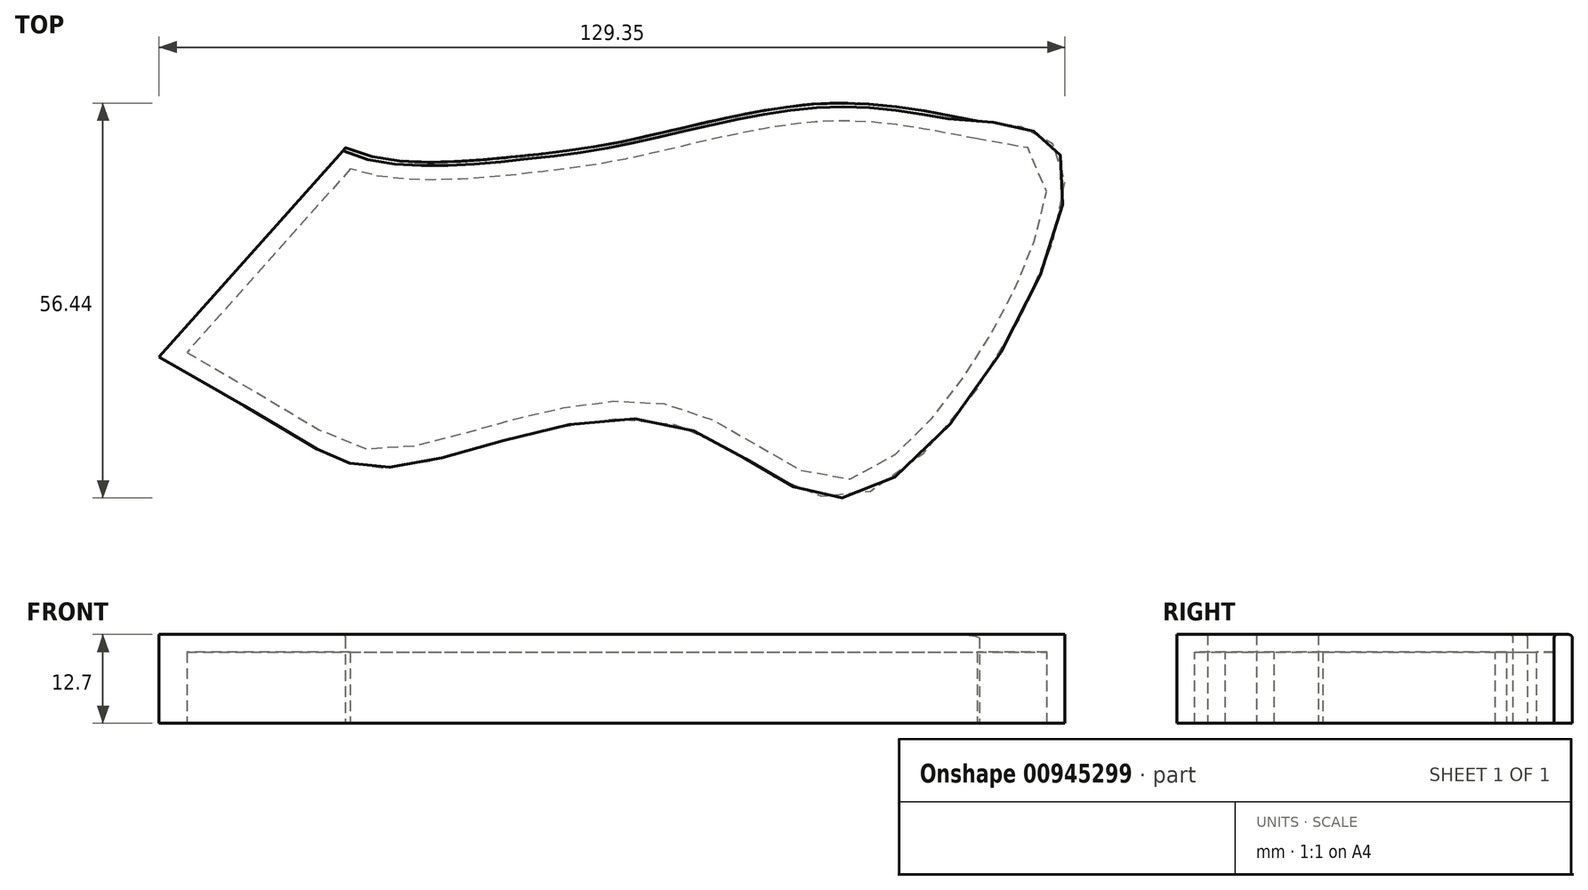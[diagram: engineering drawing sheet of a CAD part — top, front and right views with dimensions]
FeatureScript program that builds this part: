
annotation { "Feature Type Name" : "Feature", "Feature Type Description" : "" }
export const myFeature = defineFeature(function(context is Context, id is Id, definition is map)
    precondition{}
    {
        {
            var Q0;
            Q0=qCreatedBy(makeId("Top.planeOp"),FACE);
            var sketch = newSketch(context, id + "F0", { "sketchPlane" : qUnion([Q0])});
            skFitSpline(sketch, "E0", {"points": [v(22.17, 30.32) * mm, v(0, 32.85) * mm, v(-27.06, 27.79) * mm, v(-43.5, 25.31) * mm, v(-68.33, 26.52) * mm], "startDerivative": vector(-87.77, 16.35) * mm, "endDerivative": vector(-72.22, 34.8) * mm});
            skFitSpline(sketch, "E1", {"points": [v(-68.33, 26.52) * mm, v(-94.94, -3.35) * mm], "startDerivative": vector(-26.6, -29.87) * mm, "endDerivative": vector(-26.6, -29.87) * mm});
            skFitSpline(sketch, "E2", {"points": [v(-94.94, -3.35) * mm, v(-75.4, -14.75) * mm, v(-61.46, -19.1) * mm, v(-22.17, -12.76) * mm, v(5.7, -22.9) * mm, v(34.3, 23.48) * mm, v(22.17, 30.32) * mm], "startDerivative": vector(139.04, -80.08) * mm, "endDerivative": vector(-143.36, 10.67) * mm});
            skSolve(sketch);
        }
        {
            var Q0;
            Q0 = qSketchRegion(id + "F0", true);
            extrude(context, id + "F1", {"entities" : qUnion([Q0]), "depth" : 12.7 * mm, "offsetDistance" : 25.4 * mm});
        }
        {
            var Q0;
            Q0=makeQuery(id+"F1.opExtrude","CAP_EDGE",EDGE,{"disambiguationData":[OSD([sQuery(id+"F0.wireOp",EDGE,"E0")])],"isStart":false});
            fillet(context, id + "F2", {"entities" : qUnion([Q0]), "radius" : 0.5 * mm, "tangentPropagation" : true, "allowEdgeOverflow" : false});
        }
        {
            var Q0;
            Q0=makeQuery(id+"F1.opExtrude","CAP_FACE",FACE,{"disambiguationData":[OSD([sQuery(id+"F0.wireOp",EDGE,"E0"),sQuery(id+"F0.wireOp",EDGE,"E1"),sQuery(id+"F0.wireOp",EDGE,"E2")])],"isStart":true});
            shell(context, id + "F3", {"entities" : qUnion([Q0]), "thickness" : 2.54 * mm});
        }
    });
